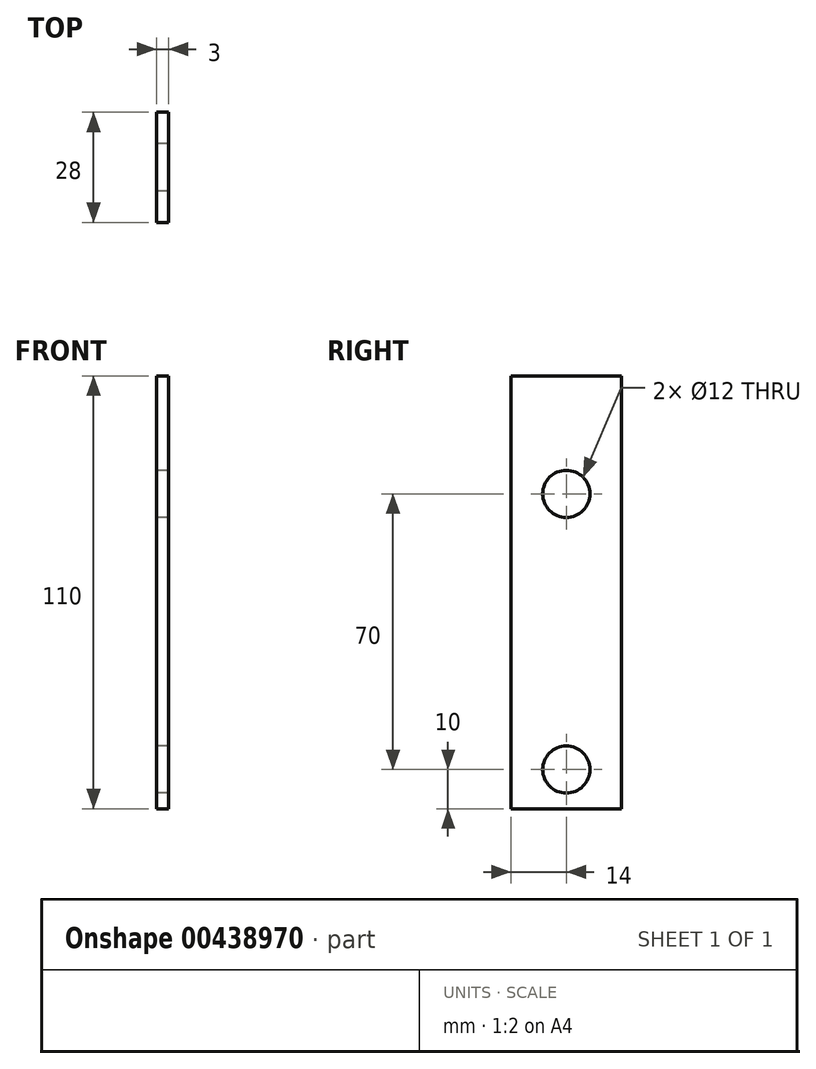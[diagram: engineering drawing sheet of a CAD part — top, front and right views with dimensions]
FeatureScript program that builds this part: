
annotation { "Feature Type Name" : "Feature", "Feature Type Description" : "" }
export const myFeature = defineFeature(function(context is Context, id is Id, definition is map)
    precondition{}
    {
        {
            var Q0;
            Q0=qCreatedBy(makeId("Right.planeOp"),FACE);
            var sketch = newSketch(context, id + "F0", { "sketchPlane" : qUnion([Q0])});
            skLineSegment(sketch, "E0.bottom", {"start": v(-14, 55) * mm, "end": v(14, 55) * mm});
            skLineSegment(sketch, "E0.top", {"start": v(-14, -55) * mm, "end": v(14, -55) * mm});
            skLineSegment(sketch, "E0.left", {"start": v(-14, 55) * mm, "end": v(-14, -55) * mm});
            skLineSegment(sketch, "E0.right", {"start": v(14, 55) * mm, "end": v(14, -55) * mm});
            skPoint(sketch, "E0.middle", {"position": v(0, 0) * mm});
            skCircle(sketch, "E1", {"center": v(0, 25) * mm, "radius": 6 * mm});
            skCircle(sketch, "E2", {"center": v(0, -45) * mm, "radius": 6 * mm});
            skSolve(sketch);
        }
        {
            var Q0;
            Q0=makeQuery(id+"F0.imprint","IMPRINT",FACE,{"disambiguationData":[TD([[makeQuery(id+"F0.imprint","IMPRINT",EDGE,{"derivedFrom":sQuery(id+"F0.wireOp",EDGE,"E0.bottom")}),-1.0]])]});
            extrude(context, id + "F1", {"entities" : qUnion([Q0]), "depth" : 3 * mm});
        }
    });
